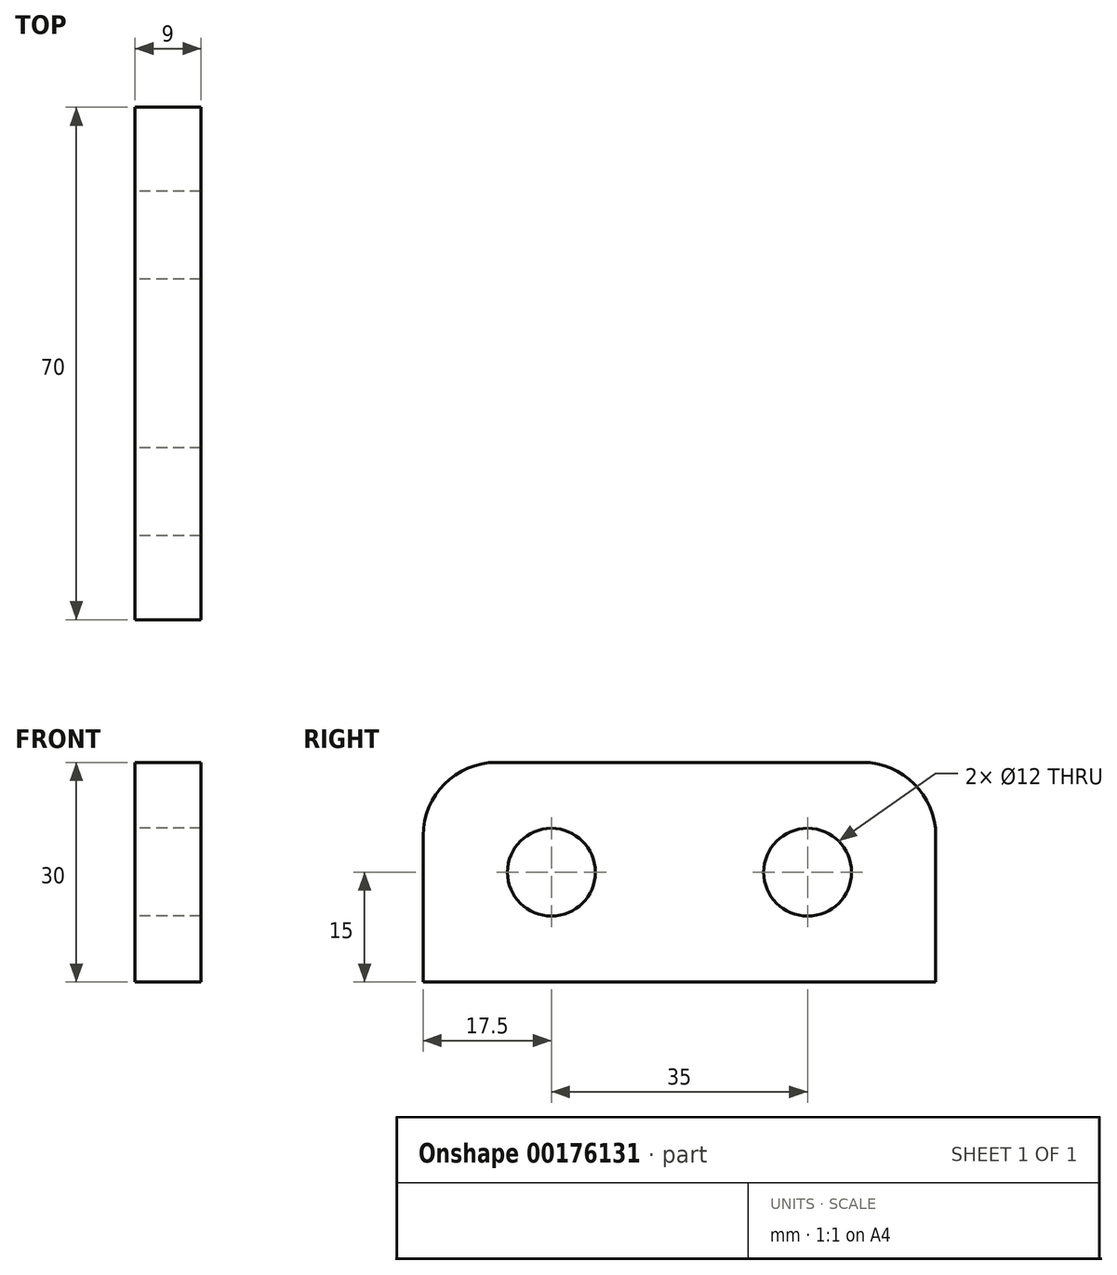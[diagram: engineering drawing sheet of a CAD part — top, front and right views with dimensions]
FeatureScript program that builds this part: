
annotation { "Feature Type Name" : "Feature", "Feature Type Description" : "" }
export const myFeature = defineFeature(function(context is Context, id is Id, definition is map)
    precondition{}
    {
        {
            var Q0;
            Q0=qCreatedBy(makeId("Right.planeOp"),FACE);
            var sketch = newSketch(context, id + "F0", { "sketchPlane" : qUnion([Q0])});
            skLineSegment(sketch, "E0.bottom", {"start": v(0, 0) * mm, "end": v(70, 0) * mm});
            skLineSegment(sketch, "E0.top", {"start": v(10, 30) * mm, "end": v(60, 30) * mm});
            skLineSegment(sketch, "E0.left", {"start": v(0, 0) * mm, "end": v(0, 20) * mm});
            skLineSegment(sketch, "E0.right", {"start": v(70, 0) * mm, "end": v(70, 20) * mm});
            skLineSegment(sketch, "E1", {"start": v(35, 30) * mm, "end": v(35, 0) * mm});
            skLineSegment(sketch, "E2", {"start": v(35, 15) * mm, "end": v(0, 15) * mm});
            skCircle(sketch, "E3", {"center": v(17.5, 15) * mm, "radius": 6 * mm});
            skLineSegment(sketch, "E4", {"start": v(35, 15) * mm, "end": v(70, 15) * mm});
            skCircle(sketch, "E5", {"center": v(52.5, 15) * mm, "radius": 6 * mm});
            skPoint(sketch, "E6.visualSharp", {"position": v(0, 30) * mm});
            skArc(sketch, "E6.filletArc", {"start": v(10, 30) * mm, "mid": v(2.93, 27.07) * mm, "end": v(0, 20) * mm});
            skPoint(sketch, "E7.visualSharp", {"position": v(70, 30) * mm});
            skArc(sketch, "E7.filletArc", {"start": v(70, 20) * mm, "mid": v(67.07, 27.07) * mm, "end": v(60, 30) * mm});
            skSolve(sketch);
        }
        {
            var Q0;
            {var subQ7=sQuery(id+"F0.wireOp",EDGE,"E6.filletArc");Q0=makeQuery(id+"F0.imprint","IMPRINT",FACE,{"disambiguationData":[TD([[makeQuery(id+"F0.imprint","IMPRINT",EDGE,{"derivedFrom":subQ7}),1.0]])]});}
            var Q1;
            {var subQ7=sQuery(id+"F0.wireOp",EDGE,"E7.filletArc");Q1=makeQuery(id+"F0.imprint","IMPRINT",FACE,{"disambiguationData":[TD([[makeQuery(id+"F0.imprint","IMPRINT",EDGE,{"derivedFrom":subQ7}),1.0]])]});}
            var Q2;
            {var subQ5=sQuery(id+"F0.wireOp",EDGE,"E0.bottom");var subQ7=sQuery(id+"F0.wireOp",EDGE,"E0.left");var subQ8=makeQuery(id+"F0.imprint","INTERSECT",VERTEX,{"derivedFrom":[subQ5,subQ7]});Q2=makeQuery(id+"F0.imprint","IMPRINT",FACE,{"disambiguationData":[TD([[makeQuery(id+"F0.imprint","IMPRINT",EDGE,{"disambiguationData":[TD([[subQ8,-1.0]])],"derivedFrom":subQ5}),1.0]])]});}
            var Q3;
            {var subQ5=sQuery(id+"F0.wireOp",EDGE,"E0.bottom");var subQ7=sQuery(id+"F0.wireOp",EDGE,"E0.right");var subQ8=makeQuery(id+"F0.imprint","INTERSECT",VERTEX,{"derivedFrom":[subQ5,subQ7]});Q3=makeQuery(id+"F0.imprint","IMPRINT",FACE,{"disambiguationData":[TD([[makeQuery(id+"F0.imprint","IMPRINT",EDGE,{"disambiguationData":[TD([[subQ8,1.0]])],"derivedFrom":subQ5}),1.0]])]});}
            extrude(context, id + "F1", {"entities" : qUnion([Q0, Q1, Q2, Q3]), "depth" : 9 * mm});
        }
    });
